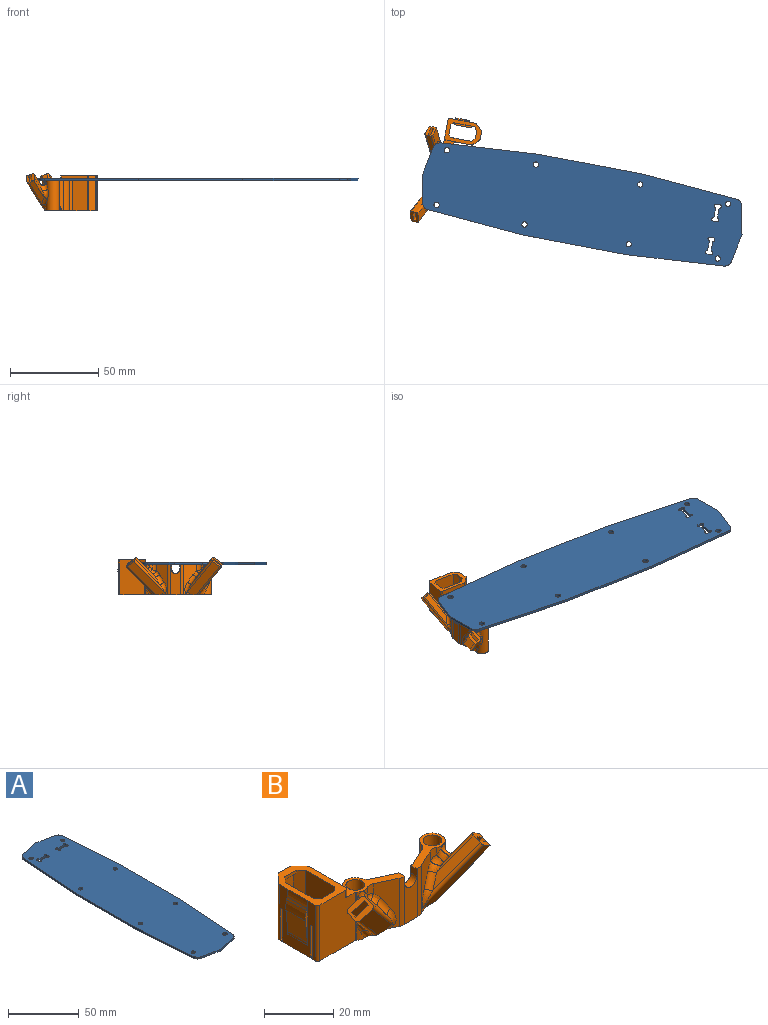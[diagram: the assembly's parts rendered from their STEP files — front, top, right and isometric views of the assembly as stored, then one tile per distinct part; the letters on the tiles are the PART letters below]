
ASSEMBLY  parts=2 mates=1
PART A: 40 faces, bbox 46.5x184x1.4 mm
  f0: plane 2x1.4mm, normal (1,0,0), area 2.8mm2, adj f1,f37,f38,f39
  f1: cylinder r=1mm len=2mm, axis (0,0,-1), area 4.4mm2, adj f0,f2,f38,f39
  f2: plane 5.7x1.4mm, normal (0,-1,0), area 8mm2, adj f1,f3,f38,f39
  f3: cylinder r=1mm len=2mm, axis (0,0,-1), area 4.4mm2, adj f2,f4,f38,f39
  f4: plane 2x1.4mm, normal (-1,0,0), area 2.8mm2, adj f3,f5,f38,f39
  f5: cylinder r=1mm len=2mm, axis (0,0,-1), area 4.4mm2, adj f4,f6,f38,f39
  f6: plane 5.7x1.4mm, normal (0,1,0), area 8mm2, adj f5,f37,f38,f39
  f7: plane 2x1.4mm, normal (-1,0,0), area 2.8mm2, adj f8,f27,f38,f39
  f8: cylinder r=1mm len=2mm, axis (0,0,-1), area 4.4mm2, adj f7,f9,f38,f39
  f9: plane 5.7x1.4mm, normal (0,1,0), area 8mm2, adj f8,f10,f38,f39
  f10: cylinder r=1mm len=2mm, axis (0,0,-1), area 4.4mm2, adj f9,f11,f38,f39
  f11: plane 2x1.4mm, normal (1,0,0), area 2.8mm2, adj f10,f12,f38,f39
  f12: cylinder r=1mm len=2mm, axis (0,0,-1), area 4.4mm2, adj f11,f13,f38,f39
  f13: plane 5.7x1.4mm, normal (0,-1,0), area 8mm2, adj f12,f27,f38,f39
  f14: cylinder r=4.33mm len=3.94mm, axis (0,0,-1), area 7.9mm2, adj f15,f36,f38,f39
  f15: plane 15.75x3mm, normal (0.19,0.98,0), area 22.4mm2, adj f14,f16,f38,f39
  f16: plane 15.75x3mm, normal (-0.19,0.98,0), area 22.4mm2, adj f15,f17,f38,f39
  f17: cylinder r=4.33mm len=3.94mm, axis (0,0,-1), area 7.9mm2, adj f16,f18,f38,f39
  f18: plane 55.04x4mm, normal (-1,0.07,0), area 77.3mm2, adj f17,f19,f38,f39
  f19: plane 60x1.4mm, normal (-1,0,0), area 84mm2, adj f18,f20,f38,f39
  f20: plane 55.04x4mm, normal (-1,-0.07,0), area 77.3mm2, adj f19,f21,f38,f39
  f21: cylinder r=4.33mm len=3.94mm, axis (0,0,-1), area 7.9mm2, adj f20,f22,f38,f39
  f22: plane 15.75x3mm, normal (-0.19,-0.98,0), area 22.4mm2, adj f21,f23,f38,f39
  f23: plane 15.75x3mm, normal (0.19,-0.98,0), area 22.4mm2, adj f22,f24,f38,f39
  f24: cylinder r=4.33mm len=3.94mm, axis (0,0,-1), area 7.9mm2, adj f23,f25,f38,f39
  f25: plane 55.04x4mm, normal (1,-0.07,0), area 77.3mm2, adj f24,f26,f38,f39
  f26: plane 60x1.4mm, normal (1,0,0), area 84mm2, adj f25,f36,f38,f39
  f27: cylinder r=1mm len=2mm, axis (0,0,-1), area 4.4mm2, adj f7,f13,f38,f39
  f28: cylinder r=1.5mm len=3mm, axis (0,0,-1), area 13.2mm2, adj f38,f39
  f29: cylinder r=1.5mm len=3mm, axis (0,0,-1), area 13.2mm2, adj f38,f39
  f30: cylinder r=1.5mm len=3mm, axis (0,0,-1), area 13.2mm2, adj f38,f39
  f31: cylinder r=1.5mm len=3mm, axis (0,0,-1), area 13.2mm2, adj f38,f39
  f32: cylinder r=1.5mm len=3mm, axis (0,0,-1), area 13.2mm2, adj f38,f39
  f33: cylinder r=1.5mm len=3mm, axis (0,0,-1), area 13.2mm2, adj f38,f39
  f34: cylinder r=1.5mm len=3mm, axis (0,0,-1), area 13.2mm2, adj f38,f39
  f35: cylinder r=1.5mm len=3mm, axis (0,0,-1), area 13.2mm2, adj f38,f39
  f36: plane 55.04x4mm, normal (1,0.07,0), area 77.3mm2, adj f14,f26,f38,f39
  f37: cylinder r=1mm len=2mm, axis (0,0,-1), area 4.4mm2, adj f0,f6,f38,f39
  f38: plane 183.96x46.5mm, normal (0,0,1), area 7744.1mm2, adj f0,f1,f2,f3,f4,f5,f6,f7
  f39: plane 183.96x46.5mm, normal (0,0,-1), area 7744.1mm2, adj f0,f1,f2,f3,f4,f5,f6,f7
PART B: 140 faces, bbox 62.6x31.8x23.8 mm
  f0: bspline ~4.04x3.66mm, area 10.3mm2, adj f3,f90,f97,f100,f125
  f1: bspline ~4.04x3.67mm, area 10.4mm2, adj f2,f64,f83,f86,f134
  f2: bspline ~4.26x3.94mm, area 7.8mm2, adj f1,f64,f86,f133
  f3: bspline ~4.36x4.02mm, area 7.9mm2, adj f0,f90,f100,f124
  f4: cylinder r=3.7mm len=5.14mm, axis (0,0,-1), area 6.7mm2, adj f32,f108,f138,f139
  f5: plane 4.51x3.02mm, normal (0.77,-0.27,0.58), area 1.2mm2, adj f6,f26,f32,f67,f78
  f6: cylinder r=1mm len=0.28mm, axis (-0.64,-0.32,0.69), area 0mm2, adj f5,f32,f78
  f7: cylinder r=1mm len=16.21mm, axis (-0.64,-0.32,0.69), area 33.8mm2, adj f9,f10,f32,f81,f139
  f8: cylinder r=1mm len=1.71mm, axis (-0.64,-0.32,0.69), area 0.2mm2, adj f27,f32,f66,f80
  f9: plane 13.22x11.06mm, normal (-0.77,0.27,-0.58), area 45.9mm2, adj f7,f81,f82,f137,f138
  f10: plane 19.76x18.83mm, normal (0,-0.91,-0.42), area 122.3mm2, adj f7,f32,f81,f84,f129
  f11: plane 17.32x16.03mm, normal (0.77,-0.27,0.58), area 43.9mm2, adj f12,f13,f32,f81
  f12: plane 21.89x19.58mm, normal (0,0.91,0.42), area 135.3mm2, adj f11,f26,f32,f68,f81
  f13: plane 20.35x20.2mm, normal (0,-0.91,-0.42), area 132.4mm2, adj f11,f26,f32,f68,f81
  f14: plane 4.51x3.01mm, normal (-0.77,-0.27,0.58), area 0.9mm2, adj f15,f23,f32,f70,f93
  f15: cylinder r=1mm len=0.28mm, axis (0.64,-0.32,0.69), area 0mm2, adj f14,f32,f93
  f16: cylinder r=1mm len=16.21mm, axis (0.64,-0.32,0.69), area 33.8mm2, adj f18,f19,f32,f95,f128
  f17: cylinder r=1mm len=1.68mm, axis (0.64,-0.32,0.69), area 0.2mm2, adj f25,f32,f69,f94
  f18: plane 13.22x11.06mm, normal (0.77,0.27,-0.58), area 45.9mm2, adj f16,f95,f96,f127
  f19: plane 19.76x18.83mm, normal (0,-0.91,-0.42), area 122.3mm2, adj f16,f32,f95,f98,f120
  f20: plane 17.32x16.03mm, normal (-0.77,-0.27,0.58), area 43.9mm2, adj f21,f22,f32,f95
  f21: plane 21.83x19.58mm, normal (0,0.91,0.42), area 135.2mm2, adj f20,f23,f32,f71,f95
  f22: plane 20.35x20.12mm, normal (0,-0.91,-0.42), area 131.8mm2, adj f20,f23,f32,f71,f95
  f23: plane 7.13x5.25mm, normal (-0.41,0.91,0), area 19mm2, adj f14,f21,f22,f24,f32,f69,f70,f71
  f24: plane 2.54x0.46mm, normal (-0.6,0.8,0), area 1.2mm2, adj f23,f25,f32,f69
  f25: plane 1.8x0.27mm, normal (-0.74,0.67,0), area 0.5mm2, adj f17,f24,f32,f69
  f26: plane 7.22x5.15mm, normal (0.42,0.91,0), area 19.1mm2, adj f5,f12,f13,f27,f32,f66,f67,f68
  f27: plane 2.2x0.58mm, normal (0.63,0.78,0), area 1.2mm2, adj f8,f26,f32,f66
  f28: plane 19.7x10.5mm, normal (0,1,0), area 187.3mm2, adj f30,f31,f32,f38,f45,f50,f52,f53
  f29: plane 11.6x2mm, normal (0,-1,0), area 22.7mm2, adj f31,f32,f33,f43,f116,f117
  f30: plane 17.8x13.31mm, normal (1,0,0), area 210.9mm2, adj f28,f33,f43,f45,f46,f50,f53,f54
  f31: plane 19.7x14.72mm, normal (-1,0,0), area 140.8mm2, adj f28,f29,f32,f42,f43,f44,f45,f54
  f32: plane 53.86x24.85mm, normal (0,0,-1), area 228.6mm2, adj f4,f5,f6,f7,f8,f10,f11,f12
  f33: plane 19.7x2.59mm, normal (0.71,-0.71,0), area 71.1mm2, adj f29,f30,f32,f39,f49,f51,f54
  f34: plane 19.7x14.72mm, normal (1,0,0), area 183.9mm2, adj f32,f54,f56,f59,f79,f107
  f35: plane 19.7x3.18mm, normal (0.71,0.71,0), area 88.5mm2, adj f32,f54,f56,f57
  f36: plane 19.7x4.14mm, normal (0,1,0), area 81.7mm2, adj f32,f54,f57,f58
  f37: plane 19.7x3.18mm, normal (-0.71,0.71,0), area 88.5mm2, adj f32,f54,f58,f61
  f38: plane 19.7x13.31mm, normal (-1,0,0), area 260.8mm2, adj f28,f32,f40,f52,f54,f55
  f39: plane 18.7x3.32mm, normal (0,-1,0), area 62mm2, adj f32,f33,f40,f49
  f40: plane 19.7x2.59mm, normal (-0.71,-0.71,0), area 71.1mm2, adj f32,f38,f39,f49,f51,f54
  f41: plane 19.7x14.4mm, normal (0,-1,0), area 273.1mm2, adj f32,f54,f59,f60,f79,f108
  f42: plane 11.3x1mm, normal (0,1,0), area 11.3mm2, adj f31,f43,f63,f117
  f43: plane 2x1.27mm, normal (0,0,-1), area 2.1mm2, adj f29,f30,f31,f42,f63
  f44: plane 11.3x1mm, normal (0,-1,0), area 11.3mm2, adj f31,f45,f62,f118
  f45: plane 2x1.27mm, normal (0,0,-1), area 2.1mm2, adj f28,f30,f31,f44,f62
  f46: plane 10.77x1mm, normal (0,0,1), area 9.8mm2, adj f30,f47,f62,f63
  f47: plane 7.31x0.75mm, normal (1,0,0), area 5.5mm2, adj f46,f48,f62,f63
  f48: plane 10.93x1.15mm, normal (0.71,0,-0.71), area 16.2mm2, adj f32,f47,f62,f63
  f49: plane 4.92x0.8mm, normal (0,0,-1), area 3.3mm2, adj f33,f39,f40,f51
  f50: plane 1.41x1.41mm, normal (0,0,-1), area 1mm2, adj f28,f30,f53
  f51: plane 4.92x1mm, normal (0,-1,0), area 4.9mm2, adj f33,f40,f49,f54
  f52: plane 1.41x1.41mm, normal (-0.71,0.71,0), area 2mm2, adj f28,f38,f54,f55
  f53: plane 1.41x1.41mm, normal (0.71,0.71,0), area 2mm2, adj f28,f30,f50,f54
  f54: plane 19.9x12.5mm, normal (0,0,1), area 110.9mm2, adj f28,f30,f31,f33,f34,f35,f36,f37
  f55: plane 1.41x1.41mm, normal (0,0,-1), area 1mm2, adj f28,f38,f52
  f56: cylinder r=1mm len=19.7mm, axis (0,0,-1), area 15.5mm2, adj f32,f34,f35,f54
  f57: cylinder r=1mm len=19.7mm, axis (0,0,-1), area 15.5mm2, adj f32,f35,f36,f54
  f58: cylinder r=1mm len=19.7mm, axis (0,0,-1), area 15.5mm2, adj f32,f36,f37,f54
  f59: cylinder r=1mm len=2.7mm, axis (0,0,-1), area 4.2mm2, adj f34,f41,f54,f79
  f60: cylinder r=1mm len=19.7mm, axis (0,0,-1), area 30.9mm2, adj f31,f32,f41,f54
  f61: cylinder r=1mm len=19.7mm, axis (0,0,-1), area 15.5mm2, adj f31,f32,f37,f54
  f62: cylinder r=2mm len=11.6mm, axis (0,0,-1), area 14.2mm2, adj f30,f44,f45,f46,f47,f48,f118,f119
  f63: cylinder r=2mm len=11.6mm, axis (0,0,-1), area 14.2mm2, adj f30,f42,f43,f46,f47,f48,f116,f117
  f64: cylinder r=3.7mm len=3.96mm, axis (0,0,-1), area 4.2mm2, adj f1,f2,f72,f79,f108,f134
  f65: plane 16.95x10.7mm, normal (0,0,1), area 48.1mm2, adj f75,f76,f89,f90,f91,f92,f93,f94
  f66: plane 3.97x3.59mm, normal (0,0.91,0.42), area 1.8mm2, adj f8,f26,f27,f67,f78,f80
  f67: cylinder r=1mm len=1.87mm, axis (-0.64,-0.32,0.69), area 0.6mm2, adj f5,f26,f66,f78
  f68: plane 20.1x17.9mm, normal (-0.77,0.27,-0.58), area 47.8mm2, adj f12,f13,f26,f81
  f69: plane 3.9x3.49mm, normal (0,0.91,0.42), area 0.9mm2, adj f17,f23,f24,f25,f70,f93,f94
  f70: cylinder r=1mm len=1.79mm, axis (0.64,-0.32,0.69), area 0.4mm2, adj f14,f23,f69,f93
  f71: plane 20.03x17.84mm, normal (0.77,0.27,-0.58), area 47.6mm2, adj f21,f22,f23,f95
  f72: cylinder r=3mm len=3.47mm, axis (0,0,-1), area 8.3mm2, adj f64,f74,f79,f133
  f73: cylinder r=3.7mm len=17mm, axis (0,0,-1), area 132.5mm2, adj f32,f79,f80,f106
  f74: plane 17.33x7.42mm, normal (-0.42,-0.91,0), area 68.4mm2, adj f32,f72,f79,f88,f129,f130,f131,f132
  f75: plane 17x5.62mm, normal (0,-1,0), area 73.2mm2, adj f32,f65,f79,f88,f102,f103,f104,f105
  f76: plane 17x5.4mm, normal (0,1,0), area 69.4mm2, adj f32,f65,f79,f87,f101,f103,f104,f105
  f77: cylinder r=2.7mm len=17mm, axis (0,0,-1), area 288.4mm2, adj f32,f79
  f78: plane 17x6.98mm, normal (0.42,0.91,0), area 104.1mm2, adj f5,f6,f32,f66,f67,f79,f80,f87
  f79: plane 19.83x11.61mm, normal (0,0,1), area 60.8mm2, adj f34,f41,f59,f64,f72,f73,f74,f75
  f80: cylinder r=3mm len=17mm, axis (0,0,-1), area 42.3mm2, adj f8,f32,f66,f73,f78,f79
  f81: plane 5.97x5.62mm, normal (-0.64,-0.32,0.69), area 24.8mm2, adj f7,f9,f10,f11,f12,f13,f68,f82
  f82: cylinder r=1mm len=10.66mm, axis (-0.64,-0.32,0.69), area 18.8mm2, adj f9,f81,f83,f136
  f83: plane 9.94x8.59mm, normal (0,0.91,0.42), area 41.6mm2, adj f1,f81,f82,f86,f134,f135
  f84: cylinder r=1mm len=18.22mm, axis (-0.64,-0.32,0.69), area 36mm2, adj f10,f81,f85,f130
  f85: plane 15.17x12.87mm, normal (0.77,-0.27,0.58), area 53.5mm2, adj f81,f84,f86,f131
  f86: cylinder r=1mm len=11.17mm, axis (-0.64,-0.32,0.69), area 17.9mm2, adj f1,f2,f81,f83,f85,f132,f133
  f87: cylinder r=2mm len=17mm, axis (0,0,1), area 14.8mm2, adj f32,f76,f78,f79
  f88: cylinder r=4mm len=17mm, axis (0,0,-1), area 29.7mm2, adj f32,f74,f75,f79
  f89: cylinder r=3mm len=3.47mm, axis (0,0,-1), area 8.3mm2, adj f65,f90,f91,f124
  f90: cylinder r=3.7mm len=17mm, axis (0,0,-1), area 239mm2, adj f0,f3,f32,f65,f89,f94,f125,f126
  f91: plane 17.33x7.42mm, normal (0.42,-0.91,0), area 68.4mm2, adj f32,f65,f89,f102,f120,f121,f122,f123
  f92: cylinder r=2.7mm len=17mm, axis (0,0,-1), area 288.4mm2, adj f32,f65
  f93: plane 17x6.98mm, normal (-0.42,0.91,0), area 104.1mm2, adj f14,f15,f32,f65,f69,f70,f94,f101
  f94: cylinder r=3mm len=17mm, axis (0,0,-1), area 42.3mm2, adj f17,f32,f65,f69,f90,f93
  f95: plane 5.97x5.62mm, normal (0.64,-0.32,0.69), area 24.8mm2, adj f16,f18,f19,f20,f21,f22,f71,f96
  f96: cylinder r=1mm len=10.53mm, axis (0.64,-0.32,0.69), area 18.2mm2, adj f18,f95,f97,f126
  f97: plane 9.55x8.61mm, normal (0,0.91,0.42), area 41.1mm2, adj f0,f95,f96,f100,f125
  f98: cylinder r=1mm len=18.22mm, axis (0.64,-0.32,0.69), area 36mm2, adj f19,f95,f99,f121
  f99: plane 15.17x12.87mm, normal (-0.77,-0.27,0.58), area 53.5mm2, adj f95,f98,f100,f122
  f100: cylinder r=1mm len=11.17mm, axis (0.64,-0.32,0.69), area 17.9mm2, adj f0,f3,f95,f97,f99,f123,f124
  f101: cylinder r=2mm len=17mm, axis (0,0,1), area 14.8mm2, adj f32,f65,f76,f93
  f102: cylinder r=4mm len=17mm, axis (0,0,-1), area 29.7mm2, adj f32,f65,f75,f91
  f103: cylinder r=2.5mm len=5mm, axis (0,-1,0), area 19.6mm2, adj f75,f76,f104,f105
  f104: plane 2.5x2.5mm, normal (1,0,0), area 6.2mm2, adj f75,f76,f79,f103
  f105: plane 2.5x2.5mm, normal (-1,0,0), area 6.2mm2, adj f65,f75,f76,f103
  f106: plane 17x0.96mm, normal (0,1,0), area 16.3mm2, adj f32,f73,f79,f107
  f107: cylinder r=2mm len=17mm, axis (0,0,1), area 53.4mm2, adj f32,f34,f79,f106
  f108: cylinder r=2mm len=17mm, axis (0,0,-1), area 6.5mm2, adj f4,f32,f41,f64,f79,f135,f136,f137
  f109: plane 8x8mm, normal (-1,0,-0.1), area 64.3mm2, adj f111,f112,f113,f114
  f110: plane 8x0.77mm, normal (-0.97,0,0.26), area 6.4mm2, adj f111,f112,f114,f115
  f111: plane 15.83x0.87mm, normal (0,1,0), area 6.9mm2, adj f31,f109,f110,f113,f114,f115
  f112: plane 15.83x0.87mm, normal (0,-1,0), area 6.9mm2, adj f31,f109,f110,f113,f114,f115
  f113: cylinder r=10mm len=8mm, axis (0,1,0), area 7.8mm2, adj f31,f109,f111,f112
  f114: cylinder r=10mm len=8mm, axis (0,-1,0), area 28.5mm2, adj f109,f110,f111,f112
  f115: cylinder r=10mm len=8mm, axis (0,1,0), area 20.7mm2, adj f54,f110,f111,f112
  f116: plane 1.19x0.3mm, normal (1,0,0), area 0.4mm2, adj f29,f32,f63,f117
  f117: plane 1.85x1.19mm, normal (0,0,1), area 1.9mm2, adj f29,f31,f42,f63,f116
  f118: plane 1.85x1.19mm, normal (0,0,1), area 1.9mm2, adj f28,f31,f44,f62,f119
  f119: plane 1.19x0.3mm, normal (1,0,0), area 0.4mm2, adj f28,f32,f62,f118
  f120: cylinder r=2mm len=2.46mm, axis (0.67,0.31,-0.67), area 2.2mm2, adj f19,f32,f91,f121
  f121: bspline ~6.33x3.81mm, area 12.7mm2, adj f91,f98,f120,f122
  f122: cylinder r=2mm len=5.46mm, axis (-0.53,-0.25,-0.81), area 17.5mm2, adj f91,f99,f121,f123
  f123: bspline ~4.12x3.3mm, area 9.7mm2, adj f91,f100,f122,f124
  f124: bspline ~4.75x4.54mm, area 8.2mm2, adj f3,f89,f100,f123
  f125: bspline ~4.45x4.23mm, area 15.8mm2, adj f0,f90,f97,f126
  f126: bspline ~7.06x3.63mm, area 14.2mm2, adj f90,f96,f125,f127
  f127: bspline ~5.79x3.72mm, area 11.6mm2, adj f18,f90,f126,f128
  f128: bspline ~5.97x4.98mm, area 11.2mm2, adj f16,f32,f90,f127
  f129: cylinder r=2mm len=2.46mm, axis (-0.67,0.31,-0.67), area 2.2mm2, adj f10,f32,f74,f130
  f130: bspline ~6.33x3.81mm, area 12.7mm2, adj f74,f84,f129,f131
  f131: cylinder r=2mm len=5.46mm, axis (0.53,-0.25,-0.81), area 17.5mm2, adj f74,f85,f130,f132
  f132: bspline ~4.12x3.3mm, area 9.6mm2, adj f74,f86,f131,f133
  f133: bspline ~4.75x4.54mm, area 8.2mm2, adj f2,f72,f86,f132
  f134: bspline ~3.67x2.11mm, area 3.5mm2, adj f1,f64,f83,f135
  f135: bspline ~5.51x4.58mm, area 10.9mm2, adj f83,f108,f134,f136
  f136: bspline ~6.51x2.71mm, area 8.7mm2, adj f82,f108,f135,f137
  f137: bspline ~3.11x2.34mm, area 2.4mm2, adj f9,f108,f136,f138
  f138: bspline ~3.66x3.01mm, area 8.1mm2, adj f4,f9,f137,f139
  f139: bspline ~5.97x4.98mm, area 11.2mm2, adj f4,f7,f32,f138
PLACE A rot(axis=(-0.77,-0.64,0),180deg) t=(-158.49,-115.47,-68.43)mm
PLACE B rot(axis=(0,0,-1),100.8deg) t=(-238.04,-100.32,-86.83)mm
MATE fastened A.f29 <-> B.f90  axis (0,0,-1) through (-240.99,-115.79,-69.83)mm
